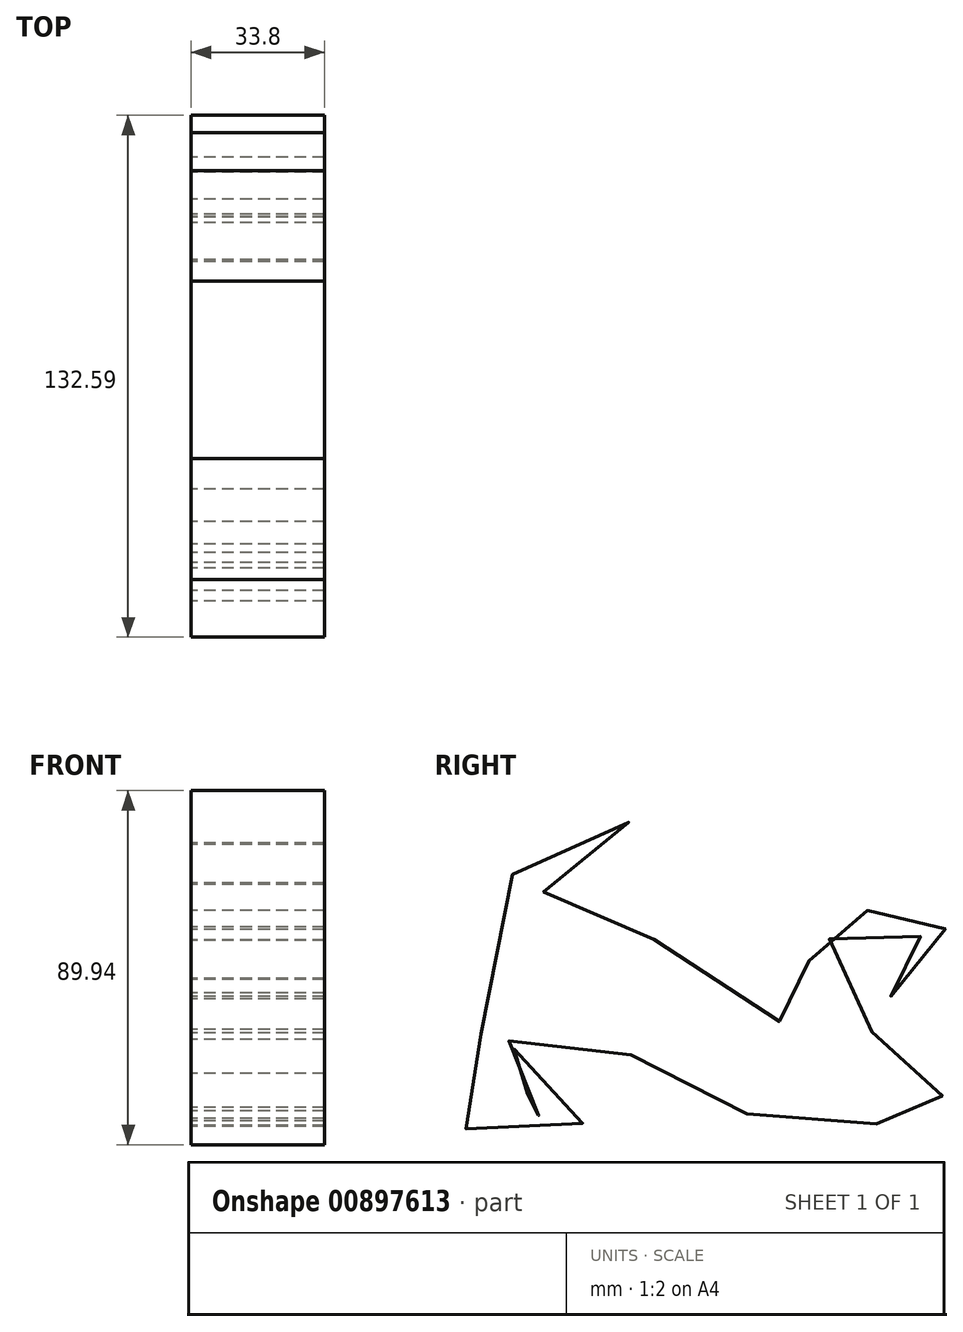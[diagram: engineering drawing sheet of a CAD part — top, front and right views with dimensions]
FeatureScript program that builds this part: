
annotation { "Feature Type Name" : "Feature", "Feature Type Description" : "" }
export const myFeature = defineFeature(function(context is Context, id is Id, definition is map)
    precondition{}
    {
        {
            var Q0;
            Q0=qCreatedBy(makeId("Right.planeOp"),FACE);
            var sketch = newSketch(context, id + "F0", { "sketchPlane" : qUnion([Q0])});
            skFitSpline(sketch, "E0", {"points": [v(-58.21, -23.94) * mm, v(-63.03, -27.9) * mm, v(-65.58, -34.13) * mm, v(-65.86, -41.22) * mm, v(-63.31, -46.88) * mm, v(-57.65, -50.28) * mm, v(-50, -51.41) * mm, v(-42.92, -51.98) * mm, v(-33.28, -47.45) * mm, v(-28.47, -37.53) * mm, v(-32.72, -27.05) * mm, v(-48.01, -26.77) * mm, v(-53.11, -31.58) * mm, v(-53.96, -38.38) * mm, v(-49.43, -43.2) * mm, v(-44.62, -42.35) * mm, v(-47.17, -37.53) * mm, v(-42.07, -34.13) * mm, v(-37.25, -35.55) * mm, v(-37.25, -40.93) * mm, v(-40.93, -43.77) * mm, v(-49.71, -45.18) * mm, v(-55.66, -40.93) * mm, v(-56.8, -35.55) * mm, v(-53.4, -27.9) * mm, v(-46.03, -23.09) * mm, v(-38.67, -23.09) * mm, v(-27.62, -24.22) * mm, v(-19.69, -29.6) * mm, v(-12.04, -35.55) * mm, v(-5.52, -40.37) * mm, v(5.24, -43.2) * mm, v(13.17, -45.18) * mm, v(23.65, -45.47) * mm, v(29.6, -42.63) * mm, v(41.5, -46.6) * mm, v(55.38, -47.17) * mm, v(65.01, -46.32) * mm, v(65.86, -41.5) * mm, v(52.55, -39.23) * mm, v(45.47, -36.4) * mm, v(39.23, -31.87) * mm, v(41.22, -28.47) * mm, v(40.62, -20.81) * mm, v(40.37, -16.57) * mm, v(33.85, -11.76) * mm, v(30.45, -5.24) * mm, v(30.17, 0) * mm, v(33.85, 2.97) * mm, v(39.23, 2.4) * mm, v(42.92, 0) * mm, v(46.6, 2.4) * mm, v(54.53, 0) * mm, v(55.95, -3.26) * mm, v(54.53, -7.8) * mm, v(50.85, -10.06) * mm, v(46.03, -10.34) * mm, v(45.75, -14.3) * mm, v(50, -13.46) * mm, v(52.26, -14.87) * mm, v(59.63, -12.04) * mm, v(61.33, 0) * mm, v(55.38, 5.8) * mm, v(52.26, 7.5) * mm, v(52.26, 14.3) * mm, v(45.18, 8.92) * mm, v(35.27, 9.2) * mm, v(31.02, 14.02) * mm, v(26.77, 5.52) * mm, v(24.5, -3.82) * mm, v(27.9, -11.19) * mm, v(29.04, -18.84) * mm, v(28.75, -23.37) * mm, v(20.82, -21.95) * mm, v(8.64, -17.42) * mm, v(-3.54, -10.9) * mm, v(-10.34, -3.54) * mm, v(-23.65, 3.26) * mm, v(-38.38, 0) * mm, v(-41.78, 6.94) * mm, v(-42.07, 15.16) * mm, v(-37.82, 22.8) * mm, v(-29.89, 24.5) * mm, v(-22.52, 25.64) * mm, v(-22.52, 36.4) * mm, v(-42.35, 32.72) * mm, v(-49.71, 19.4) * mm, v(-50.85, 0) * mm, v(-48.58, -7.22) * mm, v(-58.21, -23.94) * mm]});
            skSolve(sketch);
        }
        {
            var Q0;
            Q0=makeQuery(id+"F0.imprint","IMPRINT",FACE,{"disambiguationData":[TD([[makeQuery(id+"F0.imprint","IMPRINT",EDGE,{"derivedFrom":sQuery(id+"F0.wireOp",EDGE,"E0")}),1.0]])]});
            extrude(context, id + "F1", {"entities" : qUnion([Q0]), "endBound" : BoundingType.SYMMETRIC, "depth" : 33.8 * mm, "offsetDistance" : 25 * mm});
        }
    });
